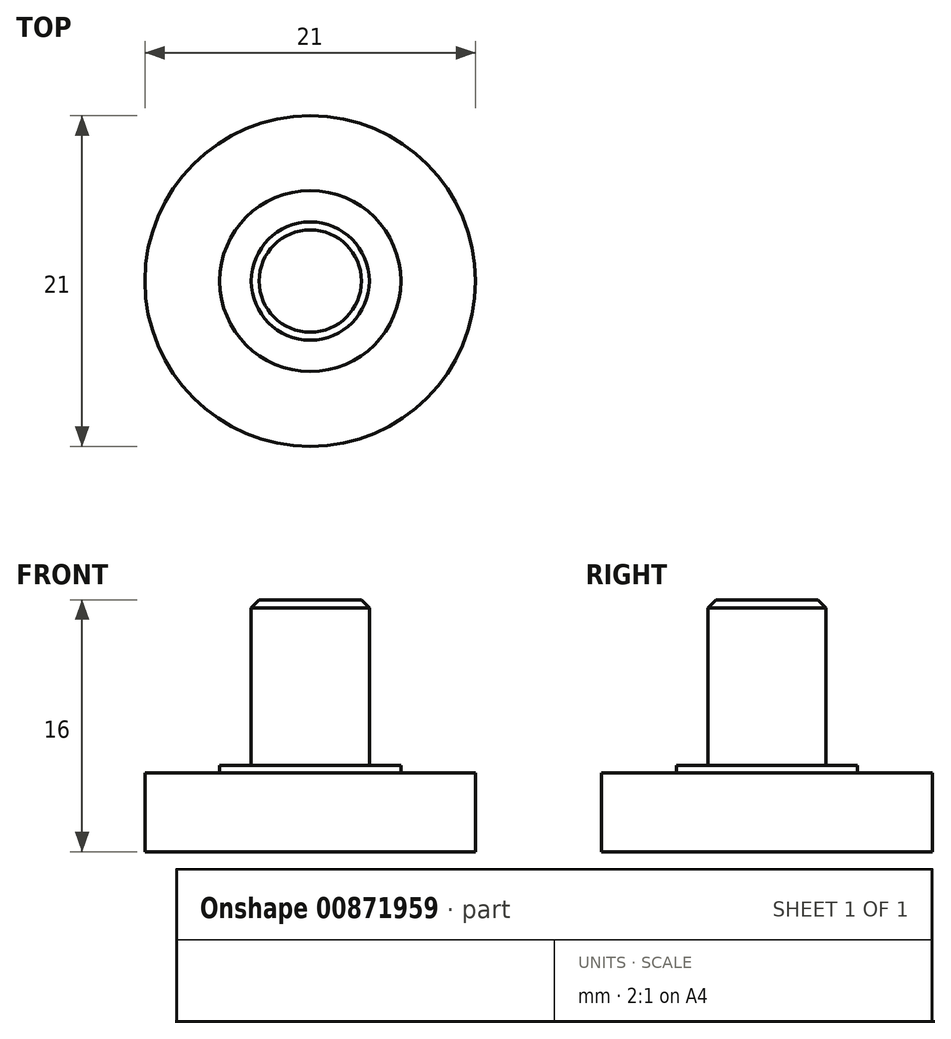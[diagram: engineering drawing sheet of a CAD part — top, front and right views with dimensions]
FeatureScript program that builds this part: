
annotation { "Feature Type Name" : "Feature", "Feature Type Description" : "" }
export const myFeature = defineFeature(function(context is Context, id is Id, definition is map)
    precondition{}
    {
        {
            var Q0;
            Q0=qCreatedBy(makeId("Top.planeOp"),FACE);
            var sketch = newSketch(context, id + "F0", { "sketchPlane" : qUnion([Q0])});
            skCircle(sketch, "E0", {"center": v(0, 0) * mm, "radius": 10.5 * mm});
            skSolve(sketch);
        }
        {
            var Q0;
            Q0 = qSketchRegion(id + "F0", true);
            extrude(context, id + "F1", {"entities" : qUnion([Q0]), "depth" : 5 * mm, "offsetDistance" : 25 * mm});
        }
        {
            var Q0;
            Q0=makeQuery(id+"F1.opExtrude","CAP_FACE",FACE,{"disambiguationData":[OSD([sQuery(id+"F0.wireOp",EDGE,"E0")])],"isStart":false});
            var sketch = newSketch(context, id + "F2", { "sketchPlane" : qUnion([Q0])});
            skCircle(sketch, "E1", {"center": v(0, 0) * mm, "radius": 5.75 * mm});
            skSolve(sketch);
        }
        {
            var Q0;
            Q0=makeQuery(id+"F2.imprint","IMPRINT",FACE,{"disambiguationData":[TD([[makeQuery(id+"F2.imprint","IMPRINT",EDGE,{"derivedFrom":sQuery(id+"F2.wireOp",EDGE,"E1")}),1.0]])]});
            extrude(context, id + "F3", {"entities" : qUnion([Q0]), "operationType" : NewBodyOperationType.ADD, "depth" : .5 * mm, "offsetDistance" : 25 * mm});
        }
        {
            var Q0;
            {var subQ0=sQuery(id+"F0.wireOp",EDGE,"E0");Q0=makeQuery(id+"F3.boolean.opBoolean","SPLIT",FACE,{"disambiguationData":[TD([makeQuery(id+"F1.opExtrude","SWEPT_FACE",FACE,{"disambiguationData":[OSD([subQ0])]})])],"derivedFrom":makeQuery(id+"F1.opExtrude","CAP_FACE",FACE,{"disambiguationData":[OSD([subQ0])],"isStart":false})});}
            var sketch = newSketch(context, id + "F4", { "sketchPlane" : qUnion([Q0])});
            skCircle(sketch, "E2", {"center": v(0, 0) * mm, "radius": 3.75 * mm});
            skSolve(sketch);
        }
        {
            var Q0;
            Q0 = qSketchRegion(id + "F4", true);
            extrude(context, id + "F5", {"entities" : qUnion([Q0]), "operationType" : NewBodyOperationType.ADD, "depth" : 11 * mm, "offsetDistance" : 25 * mm});
        }
        {
            var Q0;
            Q0=makeQuery(id+"F5.opExtrude","CAP_EDGE",EDGE,{"disambiguationData":[OSD([sQuery(id+"F4.wireOp",EDGE,"E2")])],"isStart":false});
            chamfer(context, id + "F6", {"entities" : qUnion([Q0]), "width" : .5 * mm, "tangentPropagation" : true});
        }
    });
